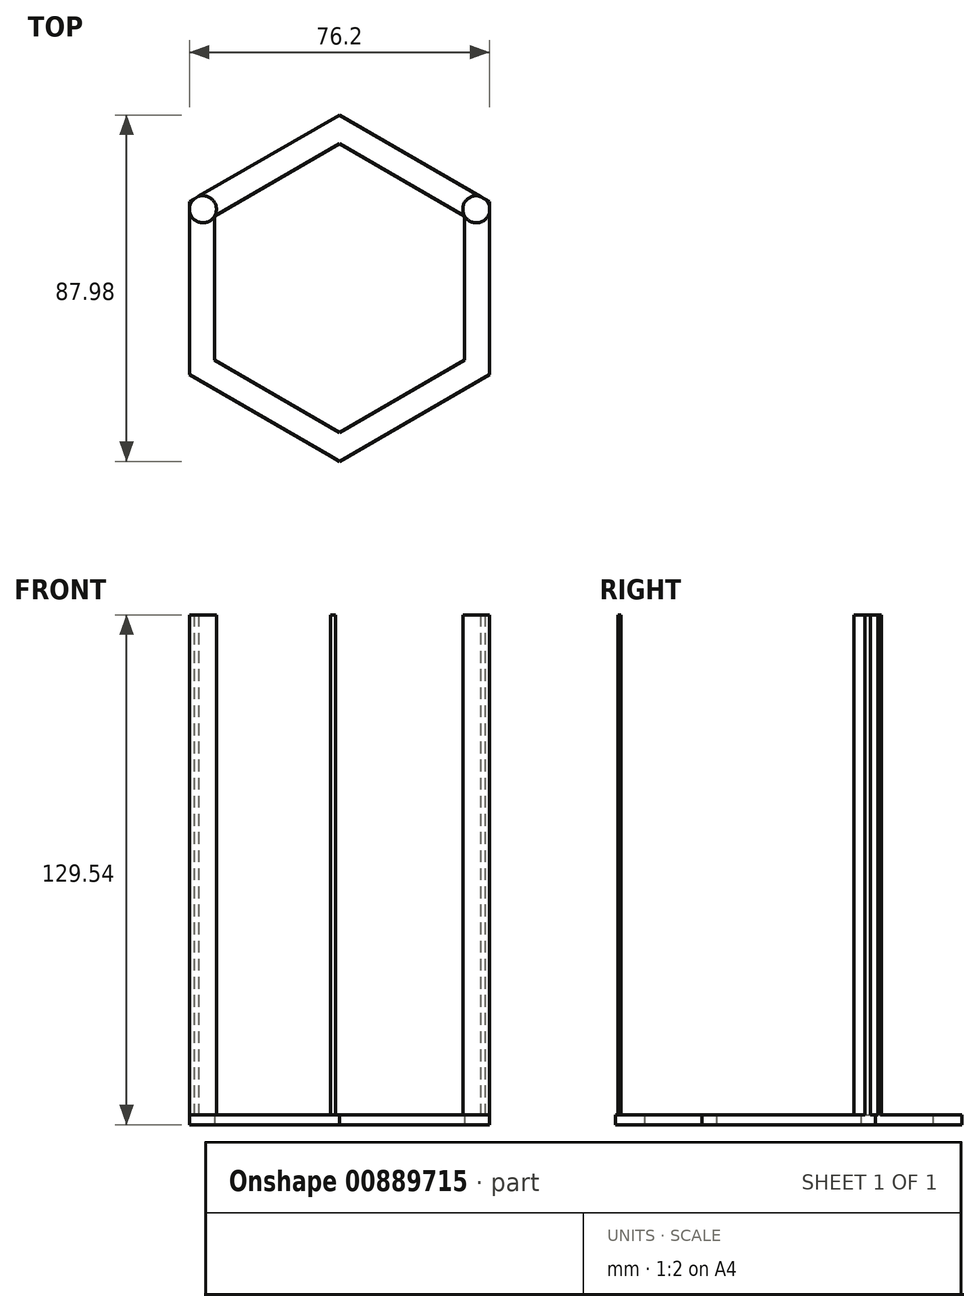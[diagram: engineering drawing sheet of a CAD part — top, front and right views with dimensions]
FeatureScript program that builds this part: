
annotation { "Feature Type Name" : "Feature", "Feature Type Description" : "" }
export const myFeature = defineFeature(function(context is Context, id is Id, definition is map)
    precondition{}
    {
        {
            var Q0;
            Q0=qCreatedBy(makeId("Top.planeOp"),FACE);
            var sketch = newSketch(context, id + "F0", { "sketchPlane" : qUnion([Q0])});
            skCircle(sketch, "E0.cCircle", {"center": v(0, 0) * mm, "radius": 31.75 * mm, "construction": true});
            skLineSegment(sketch, "E0.0", {"start": v(31.75, 18.33) * mm, "end": v(31.75, -18.33) * mm});
            skLineSegment(sketch, "E0.1", {"start": v(31.75, -18.33) * mm, "end": v(0, -36.66) * mm});
            skLineSegment(sketch, "E0.2", {"start": v(0, -36.66) * mm, "end": v(-31.75, -18.33) * mm});
            skLineSegment(sketch, "E0.3", {"start": v(-31.75, -18.33) * mm, "end": v(-31.75, 18.33) * mm});
            skLineSegment(sketch, "E0.4", {"start": v(-31.75, 18.33) * mm, "end": v(0, 36.66) * mm});
            skLineSegment(sketch, "E0.5", {"start": v(0, 36.66) * mm, "end": v(31.75, 18.33) * mm});
            skPoint(sketch, "E0.0.midPoint", {"position": v(31.75, 0) * mm});
            skLineSegment(sketch, "E1.0", {"start": v(3.17, 42.16) * mm, "end": v(34.92, 23.83) * mm});
            skLineSegment(sketch, "E2.0", {"start": v(0, 44) * mm, "end": v(38.1, 22) * mm});
            skLineSegment(sketch, "E2.1", {"start": v(38.1, -22) * mm, "end": v(0, -44) * mm});
            skLineSegment(sketch, "E2.2", {"start": v(0, -44) * mm, "end": v(-38.1, -22) * mm});
            skLineSegment(sketch, "E2.3", {"start": v(38.1, 22) * mm, "end": v(38.1, -22) * mm});
            skLineSegment(sketch, "E2.4", {"start": v(-38.1, -22) * mm, "end": v(-38.1, 22) * mm});
            skLineSegment(sketch, "E2.5", {"start": v(-38.1, 22) * mm, "end": v(0, 44) * mm});
            skSolve(sketch);
        }
        {
            var Q0;
            Q0=makeQuery(id+"F0.imprint","IMPRINT",FACE,{"disambiguationData":[TD([[makeQuery(id+"F0.imprint","IMPRINT",EDGE,{"derivedFrom":sQuery(id+"F0.wireOp",EDGE,"E0.0")}),1.0]])]});
            extrude(context, id + "F1", {"entities" : qUnion([Q0]), "depth" : 2.54 * mm, "offsetDistance" : 25.4 * mm});
        }
        {
            var Q0;
            Q0=makeQuery(id+"F1.opExtrude","CAP_FACE",FACE,{"disambiguationData":[OSD([sQuery(id+"F0.wireOp",EDGE,"E0.0"),sQuery(id+"F0.wireOp",EDGE,"E0.1"),sQuery(id+"F0.wireOp",EDGE,"E0.2"),sQuery(id+"F0.wireOp",EDGE,"E0.3"),sQuery(id+"F0.wireOp",EDGE,"E0.4"),sQuery(id+"F0.wireOp",EDGE,"E0.5"),sQuery(id+"F0.wireOp",EDGE,"E2.0"),sQuery(id+"F0.wireOp",EDGE,"E2.1"),sQuery(id+"F0.wireOp",EDGE,"E2.2"),sQuery(id+"F0.wireOp",EDGE,"E2.3"),sQuery(id+"F0.wireOp",EDGE,"E2.4"),sQuery(id+"F0.wireOp",EDGE,"E2.5")])],"isStart":false});
            var sketch = newSketch(context, id + "F2", { "sketchPlane" : qUnion([Q0])});
            skCircle(sketch, "E3", {"center": v(-34.73, 20.06) * mm, "radius": 3.44 * mm});
            skPoint(sketch, "E3.first.point", {"position": v(-35.79, 23.33) * mm});
            skPoint(sketch, "E3.second.point", {"position": v(-38.1, 19.38) * mm});
            skPoint(sketch, "E3.third.point", {"position": v(-31.75, 18.33) * mm});
            skCircle(sketch, "E4.1.0", {"center": v(0, -40.1) * mm, "radius": 3.44 * mm});
            skCircle(sketch, "E4.2.0", {"center": v(34.73, 20.04) * mm, "radius": 3.44 * mm});
            skPoint(sketch, "E4.center", {"position": v(0, 0) * mm});
            skSolve(sketch);
        }
        {
            var Q0;
            {var subQ0=sQuery(id+"F2.wireOp",EDGE,"E3");var subQ5=makeQuery(id+"F1.opExtrude","CAP_EDGE",EDGE,{"disambiguationData":[OSD([sQuery(id+"F0.wireOp",EDGE,"E2.5")])],"isStart":false});var subQ7=makeQuery(id+"F2.imprint","INTERSECT",VERTEX,{"disambiguationData":[OD(0.0)],"derivedFrom":[subQ5,subQ0]});Q0=makeQuery(id+"F2.imprint","IMPRINT",FACE,{"disambiguationData":[TD([[makeQuery(id+"F2.imprint","IMPRINT",EDGE,{"disambiguationData":[TD([[subQ7,-1.0]])],"derivedFrom":subQ0}),1.0]])]});}
            var Q1;
            {var subQ0=sQuery(id+"F2.wireOp",EDGE,"E4.2.0");var subQ2=makeQuery(id+"F1.opExtrude","CAP_EDGE",EDGE,{"disambiguationData":[OSD([sQuery(id+"F0.wireOp",EDGE,"E2.3")])],"isStart":false});var subQ7=makeQuery(id+"F2.imprint","INTERSECT",VERTEX,{"disambiguationData":[OD(0.0)],"derivedFrom":[subQ2,subQ0]});Q1=makeQuery(id+"F2.imprint","IMPRINT",FACE,{"disambiguationData":[TD([[makeQuery(id+"F2.imprint","IMPRINT",EDGE,{"disambiguationData":[TD([[subQ7,-1.0]])],"derivedFrom":subQ0}),1.0]])]});}
            var Q2;
            {var subQ0=sQuery(id+"F2.wireOp",EDGE,"E4.1.0");var subQ2=makeQuery(id+"F1.opExtrude","CAP_EDGE",EDGE,{"disambiguationData":[OSD([sQuery(id+"F0.wireOp",EDGE,"E2.2")])],"isStart":false});var subQ7=makeQuery(id+"F2.imprint","INTERSECT",VERTEX,{"disambiguationData":[OD(0.0)],"derivedFrom":[subQ2,subQ0]});Q2=makeQuery(id+"F2.imprint","IMPRINT",FACE,{"disambiguationData":[TD([[makeQuery(id+"F2.imprint","IMPRINT",EDGE,{"disambiguationData":[TD([[subQ7,-1.0]])],"derivedFrom":subQ0}),1.0]])]});}
            extrude(context, id + "F3", {"entities" : qUnion([Q0, Q1, Q2]), "operationType" : NewBodyOperationType.ADD, "depth" : 127 * mm, "offsetDistance" : 25.4 * mm});
        }
    });
